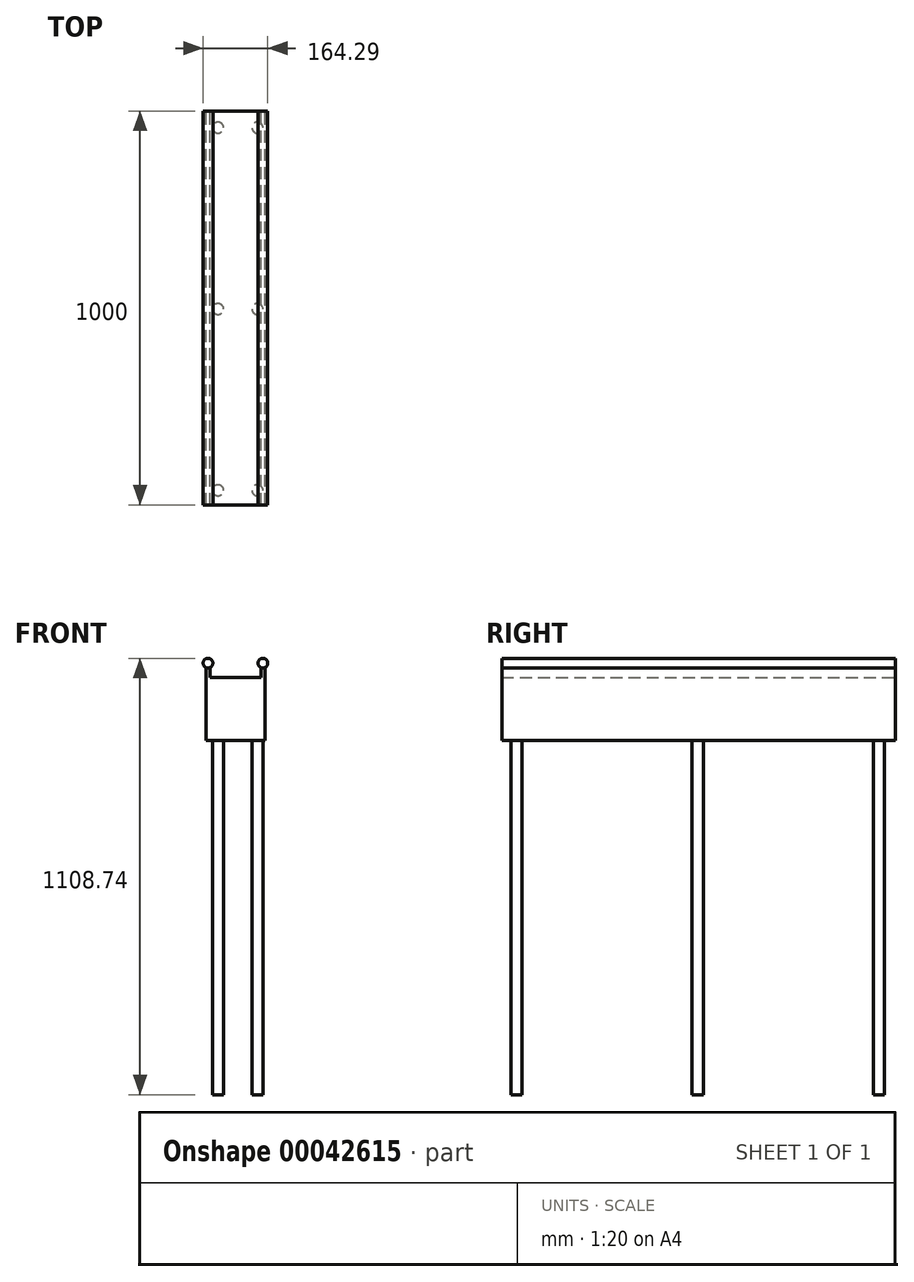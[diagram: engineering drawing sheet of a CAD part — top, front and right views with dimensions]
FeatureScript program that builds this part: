
annotation { "Feature Type Name" : "Feature", "Feature Type Description" : "" }
export const myFeature = defineFeature(function(context is Context, id is Id, definition is map)
    precondition{}
    {
        {
            var Q0;
            Q0=qCreatedBy(makeId("Front.planeOp"),FACE);
            var sketch = newSketch(context, id + "F0", { "sketchPlane" : qUnion([Q0])});
            skLineSegment(sketch, "E0.bottom", {"start": v(-74.59, 77.82) * mm, "end": v(75.41, 77.82) * mm});
            skLineSegment(sketch, "E0.top", {"start": v(-74.59, -81.55) * mm, "end": v(75.41, -81.55) * mm});
            skLineSegment(sketch, "E0.left", {"start": v(-74.59, 77.82) * mm, "end": v(-74.59, -81.55) * mm});
            skLineSegment(sketch, "E0.right", {"start": v(75.41, 77.82) * mm, "end": v(75.41, -81.55) * mm});
            skLineSegment(sketch, "E1.bottom", {"start": v(-74.59, 77.82) * mm, "end": v(-64.2, 77.82) * mm});
            skLineSegment(sketch, "E1.top", {"start": v(-74.59, 102.52) * mm, "end": v(-64.2, 102.52) * mm});
            skLineSegment(sketch, "E1.left", {"start": v(-74.59, 77.82) * mm, "end": v(-74.59, 102.52) * mm});
            skLineSegment(sketch, "E1.right", {"start": v(-64.2, 77.82) * mm, "end": v(-64.2, 102.52) * mm});
            skLineSegment(sketch, "E2.bottom", {"start": v(75.41, 77.82) * mm, "end": v(65.03, 77.82) * mm});
            skLineSegment(sketch, "E2.top", {"start": v(75.41, 102.52) * mm, "end": v(65.03, 102.52) * mm});
            skLineSegment(sketch, "E2.left", {"start": v(75.41, 77.82) * mm, "end": v(75.41, 102.52) * mm});
            skLineSegment(sketch, "E2.right", {"start": v(65.03, 77.82) * mm, "end": v(65.03, 102.52) * mm});
            skLineSegment(sketch, "E3", {"start": v(-69.4, 102.52) * mm, "end": v(-69.4, 114.86) * mm, "construction": true});
            skPoint(sketch, "E3.endSnap0", {"position": v(-69.4, 102.52) * mm});
            skCircle(sketch, "E4", {"center": v(-69.4, 114.86) * mm, "radius": 12.34 * mm});
            skLineSegment(sketch, "E5", {"start": v(0.41, 77.82) * mm, "end": v(0.41, -81.55) * mm, "construction": true});
            skCircle(sketch, "E6.MirrorC", {"center": v(70.22, 114.86) * mm, "radius": 12.34 * mm});
            skSolve(sketch);
        }
        {
            var Q0;
            Q0 = qSketchRegion(id + "F0", true);
            extrude(context, id + "F1", {"entities" : qUnion([Q0]), "depth" : 1000 * mm});
        }
        {
            var Q0;
            Q0=makeQuery(id+"F1.opExtrude","SWEPT_FACE",FACE,{"disambiguationData":[OSD([sQuery(id+"F0.wireOp",EDGE,"E0.top")])]});
            var sketch = newSketch(context, id + "F2", { "sketchPlane" : qUnion([Q0])});
            skCircle(sketch, "E7", {"center": v(56.18, 41.74) * mm, "radius": 14.06 * mm});
            skCircle(sketch, "E8.0.1.0", {"center": v(56.18, 502.55) * mm, "radius": 14.06 * mm});
            skCircle(sketch, "E8.0.2.0", {"center": v(56.18, 963.37) * mm, "radius": 14.06 * mm});
            skCircle(sketch, "E8.1.0.0", {"center": v(-43.88, 41.74) * mm, "radius": 14.06 * mm});
            skCircle(sketch, "E8.1.1.0", {"center": v(-43.88, 502.55) * mm, "radius": 14.06 * mm});
            skCircle(sketch, "E8.1.2.0", {"center": v(-43.88, 963.37) * mm, "radius": 14.06 * mm});
            skLineSegment(sketch, "E8.direction1", {"start": v(56.18, 41.74) * mm, "end": v(-43.88, 41.74) * mm, "construction": true});
            skLineSegment(sketch, "E8.direction2", {"start": v(56.18, 41.74) * mm, "end": v(56.18, 502.55) * mm, "construction": true});
            skSolve(sketch);
        }
        {
            var Q0;
            Q0 = qSketchRegion(id + "F2", true);
            extrude(context, id + "F3", {"entities" : qUnion([Q0]), "operationType" : NewBodyOperationType.ADD, "depth" : 900 * mm});
        }
    });
